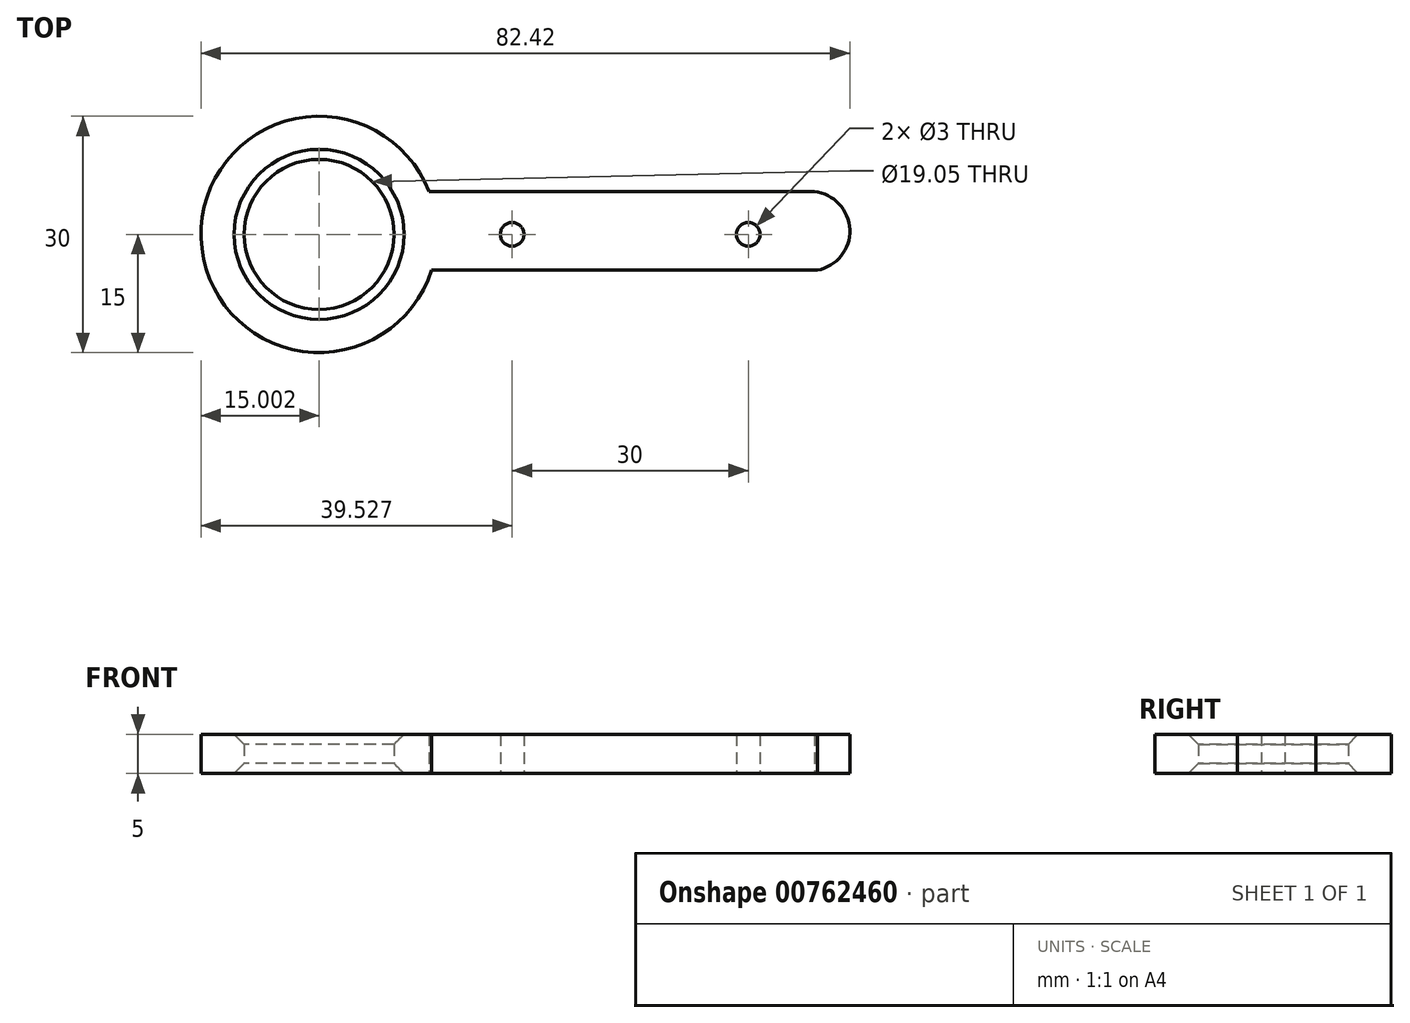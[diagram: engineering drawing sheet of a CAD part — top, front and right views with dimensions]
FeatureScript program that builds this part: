
annotation { "Feature Type Name" : "Feature", "Feature Type Description" : "" }
export const myFeature = defineFeature(function(context is Context, id is Id, definition is map)
    precondition{}
    {
        {
            var Q0;
            Q0=qCreatedBy(makeId("Top.planeOp"),FACE);
            var sketch = newSketch(context, id + "F0", { "sketchPlane" : qUnion([Q0])});
            skCircle(sketch, "E0", {"center": v(14.6, 0) * mm, "radius": 15 * mm});
            skLineSegment(sketch, "E1.bottom", {"start": v(0.62, 5.45) * mm, "end": v(-69.38, 5.45) * mm});
            skLineSegment(sketch, "E1.top", {"start": v(0.62, -4.55) * mm, "end": v(-69.38, -4.55) * mm});
            skLineSegment(sketch, "E1.left", {"start": v(0.62, 5.45) * mm, "end": v(0.62, -4.55) * mm});
            skLineSegment(sketch, "E1.right", {"start": v(-69.38, 5.45) * mm, "end": v(-69.38, -4.55) * mm});
            skCircle(sketch, "E2", {"center": v(14.6, 0) * mm, "radius": 9 * mm});
            skCircle(sketch, "E3", {"center": v(-20.4, 0) * mm, "radius": 1.5 * mm});
            skCircle(sketch, "E4", {"center": v(-50.4, 0) * mm, "radius": 1.5 * mm});
            skCircle(sketch, "E5", {"center": v(-74.93, 0) * mm, "radius": 9.53 * mm});
            skCircle(sketch, "E6", {"center": v(-74.93, 0) * mm, "radius": 15 * mm});
            skArc(sketch, "E7", {"start": v(-11.63, -4.55) * mm, "mid": v(-7.51, 0.6) * mm, "end": v(-12, 5.45) * mm});
            skSolve(sketch);
        }
        {
            var Q0;
            {var subQ0=sQuery(id+"F0.wireOp",EDGE,"E6");var subQ1=sQuery(id+"F0.wireOp",EDGE,"E1.bottom");var subQ2=makeQuery(id+"F0.imprint","INTERSECT",VERTEX,{"derivedFrom":[subQ1,subQ0]});Q0=makeQuery(id+"F0.imprint","IMPRINT",FACE,{"disambiguationData":[TD([[makeQuery(id+"F0.imprint","IMPRINT",EDGE,{"disambiguationData":[TD([[subQ2,-1.0]])],"derivedFrom":subQ1}),-1.0]])]});}
            var Q1;
            {var subQ0=sQuery(id+"F0.wireOp",EDGE,"E6");var subQ1=sQuery(id+"F0.wireOp",EDGE,"E1.bottom");var subQ2=makeQuery(id+"F0.imprint","INTERSECT",VERTEX,{"derivedFrom":[subQ1,subQ0]});Q1=makeQuery(id+"F0.imprint","IMPRINT",FACE,{"disambiguationData":[TD([[makeQuery(id+"F0.imprint","IMPRINT",EDGE,{"disambiguationData":[TD([[subQ2,-1.0]])],"derivedFrom":subQ1}),1.0]])]});}
            var Q2;
            Q2=makeQuery(id+"F0.imprint","IMPRINT",FACE,{"disambiguationData":[TD([[makeQuery(id+"F0.imprint","IMPRINT",EDGE,{"derivedFrom":sQuery(id+"F0.wireOp",EDGE,"E3")}),-1.0]])]});
            extrude(context, id + "F1", {"entities" : qUnion([Q0, Q1, Q2]), "depth" : 5 * mm, "offsetDistance" : 25.4 * mm});
        }
        {
            var Q0;
            Q0=makeQuery(id+"F1.opExtrude","CAP_EDGE",EDGE,{"disambiguationData":[OSD([sQuery(id+"F0.wireOp",EDGE,"E5")])],"isStart":false});
            var Q1;
            Q1=makeQuery(id+"F1.opExtrude","CAP_EDGE",EDGE,{"disambiguationData":[OSD([sQuery(id+"F0.wireOp",EDGE,"E5")])],"isStart":true});
            chamfer(context, id + "F2", {"entities" : qUnion([Q0, Q1]), "width" : 1.27 * mm, "tangentPropagation" : true});
        }
    });
